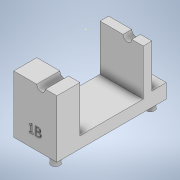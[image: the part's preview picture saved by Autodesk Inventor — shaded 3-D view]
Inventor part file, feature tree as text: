
AUTODESK INVENTOR PART (.ipt)
format: ipt  version: 2021 (Build 250183000, 183)  size: 205,824 bytes
history: native  units: mm
features: sketch x7, extrude x5, emboss x1
ambient origin geometry x8: Origin, YZ Plane, XZ Plane, XY Plane, X Axis, Y Axis, Z Axis, Center Point
bodies: Solid1 (feature_tree)
feature tree (13):
  extrude  "Extrusion1"  Depth=15.0mm TaperAngle=0.0deg
  extrude  "Extrusion2"  Depth=2.5mm
  extrude  "Extrusion3"  Depth=33.0mm
  extrude  "Extrusion4"  Depth=3.0mm
  sketch  "Sketch5"  dims[d10=3.0mm d11=0.0mm d12=8.0mm]
  extrude  "Extrusion5"  Depth=8.0mm
  emboss  "Emboss1"
  sketch  "Sketch1"  dims[d1=20.003mm d2=15.0mm d3=0.0mm]
  sketch  "Sketch2"  dims[d4=3.0mm d5=2.5mm]
  sketch  "Sketch3"  dims[d6=3.0mm d7=33.0mm]
  sketch  "Sketch4"  dims[d8=3.0mm d9=3.0mm]
  sketch  "Sketch6"  dims[d13=8.0mm]
  sketch  "Sketch7"  dims[d14=25.0mm d15=0.0mm d16=0.0mm d17=3.0mm d18=5.481mm d19=0.0mm d20=0.0mm d21=5.0mm d22=5.0mm d23=0.0mm d24=1.0mm d25=0.0mm d26=13.0mm]
